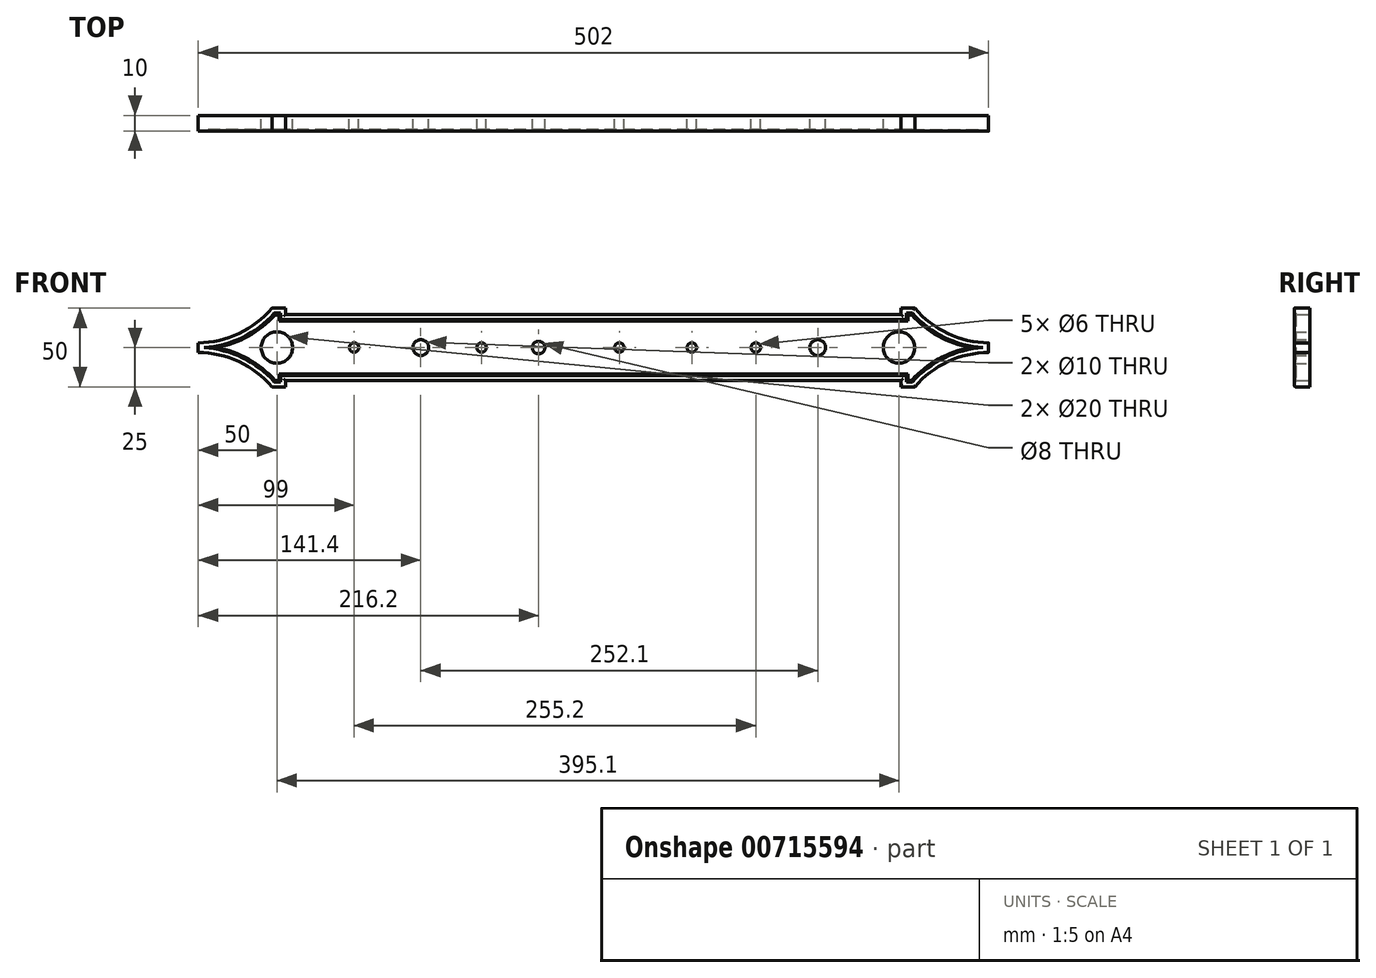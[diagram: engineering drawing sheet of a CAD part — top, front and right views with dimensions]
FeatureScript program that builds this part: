
annotation { "Feature Type Name" : "Feature", "Feature Type Description" : "" }
export const myFeature = defineFeature(function(context is Context, id is Id, definition is map)
    precondition{}
    {
        {
            var Q0;
            Q0=qCreatedBy(makeId("Front.planeOp"),FACE);
            var sketch = newSketch(context, id + "F0", { "sketchPlane" : qUnion([Q0])});
            skLineSegment(sketch, "E0.bottom", {"start": v(204.1, -25) * mm, "end": v(195.5, -25) * mm});
            skLineSegment(sketch, "E0.top", {"start": v(204.1, 25) * mm, "end": v(195.5, 25) * mm});
            skLineSegment(sketch, "E0.left", {"start": v(251, -3.05) * mm, "end": v(251, 3.05) * mm});
            skLineSegment(sketch, "E0.right", {"start": v(-251, -3.05) * mm, "end": v(-251, 3.05) * mm});
            skPoint(sketch, "E0.middle", {"position": v(0, 0) * mm});
            skLineSegment(sketch, "E1", {"start": v(-251, 3.05) * mm, "end": v(-251, -3.05) * mm});
            skLineSegment(sketch, "E2", {"start": v(251, 3.05) * mm, "end": v(251, -3.05) * mm});
            skLineSegment(sketch, "E3", {"start": v(-204.1, 25) * mm, "end": v(-195.5, 25) * mm});
            skLineSegment(sketch, "E4", {"start": v(-195.5, -25) * mm, "end": v(-204.1, -25) * mm});
            skArc(sketch, "E5", {"start": v(-251, 3.05) * mm, "mid": v(-225.17, 8.94) * mm, "end": v(-204.1, 25) * mm});
            skArc(sketch, "E6", {"start": v(-204.1, -25) * mm, "mid": v(-225.17, -8.94) * mm, "end": v(-251, -3.05) * mm});
            skPoint(sketch, "E7.orphan", {"position": v(-251, 25) * mm});
            skPoint(sketch, "E8.orphan", {"position": v(-251, -25) * mm});
            skArc(sketch, "E9", {"start": v(204.1, 25) * mm, "mid": v(225.17, 8.94) * mm, "end": v(251, 3.05) * mm});
            skArc(sketch, "E10", {"start": v(251, -3.05) * mm, "mid": v(225.17, -8.94) * mm, "end": v(204.1, -25) * mm});
            skPoint(sketch, "E11.orphan", {"position": v(251, 25) * mm});
            skPoint(sketch, "E12.orphan", {"position": v(251, -25) * mm});
            skLineSegment(sketch, "E13", {"start": v(195.5, 25) * mm, "end": v(195.5, 21) * mm});
            skLineSegment(sketch, "E14", {"start": v(195.5, -25) * mm, "end": v(195.5, -21) * mm});
            skLineSegment(sketch, "E15", {"start": v(-195.5, -25) * mm, "end": v(-195.5, -21) * mm});
            skLineSegment(sketch, "E16", {"start": v(-195.5, 25) * mm, "end": v(-195.5, 21) * mm});
            skLineSegment(sketch, "E17", {"start": v(-195.5, 21) * mm, "end": v(195.5, 21) * mm});
            skLineSegment(sketch, "E18", {"start": v(195.5, -21) * mm, "end": v(-195.5, -21) * mm});
            skLineSegment(sketch, "E19.trimOffspring", {"start": v(-195.5, 25) * mm, "end": v(-204.1, 25) * mm});
            skCircle(sketch, "E20", {"center": v(-201, 0) * mm, "radius": 10 * mm});
            skCircle(sketch, "E21", {"center": v(194.1, 0) * mm, "radius": 10 * mm});
            skCircle(sketch, "E22", {"center": v(142.5, 0) * mm, "radius": 5 * mm});
            skCircle(sketch, "E23", {"center": v(103.2, 0) * mm, "radius": 3 * mm});
            skCircle(sketch, "E24", {"center": v(62.5, 0) * mm, "radius": 3 * mm});
            skCircle(sketch, "E25", {"center": v(16.5, 0) * mm, "radius": 3 * mm});
            skCircle(sketch, "E26", {"center": v(-34.8, 0) * mm, "radius": 4 * mm});
            skCircle(sketch, "E27", {"center": v(-71, 0) * mm, "radius": 3 * mm});
            skCircle(sketch, "E28", {"center": v(-109.6, 0) * mm, "radius": 5 * mm});
            skCircle(sketch, "E29", {"center": v(-152, 0) * mm, "radius": 3 * mm});
            skLineSegment(sketch, "E30.0", {"start": v(-198.7, 21.8) * mm, "end": v(-198.7, 17.8) * mm});
            skLineSegment(sketch, "E30.1", {"start": v(-198.7, 21.8) * mm, "end": v(-202.65, 21.8) * mm});
            skArc(sketch, "E30.2", {"start": v(-247.32, 0) * mm, "mid": v(-222.84, 6.52) * mm, "end": v(-202.65, 21.8) * mm});
            skArc(sketch, "E30.4", {"start": v(-202.65, -21.81) * mm, "mid": v(-222.84, -6.52) * mm, "end": v(-247.32, 0) * mm});
            skArc(sketch, "E30.6", {"start": v(202.65, 21.81) * mm, "mid": v(222.84, 6.52) * mm, "end": v(247.32, 0) * mm});
            skLineSegment(sketch, "E30.7", {"start": v(202.65, 21.81) * mm, "end": v(198.7, 21.81) * mm});
            skLineSegment(sketch, "E30.8", {"start": v(198.7, 21.81) * mm, "end": v(198.7, 17.81) * mm});
            skArc(sketch, "E30.9", {"start": v(247.32, 0) * mm, "mid": v(222.84, -6.52) * mm, "end": v(202.65, -21.81) * mm});
            skLineSegment(sketch, "E30.10", {"start": v(202.65, -21.8) * mm, "end": v(198.7, -21.8) * mm});
            skLineSegment(sketch, "E30.11", {"start": v(198.7, -21.8) * mm, "end": v(198.7, -17.8) * mm});
            skLineSegment(sketch, "E30.12", {"start": v(198.7, -17.8) * mm, "end": v(-198.7, -17.81) * mm});
            skLineSegment(sketch, "E30.13", {"start": v(-198.7, -21.81) * mm, "end": v(-198.7, -17.81) * mm});
            skLineSegment(sketch, "E30.14", {"start": v(-198.7, 17.8) * mm, "end": v(198.7, 17.81) * mm});
            skLineSegment(sketch, "E30.15", {"start": v(-198.7, -21.81) * mm, "end": v(-202.65, -21.81) * mm});
            skLineSegment(sketch, "E31.0", {"start": v(199.7, 20.81) * mm, "end": v(199.7, 16.81) * mm});
            skLineSegment(sketch, "E31.1", {"start": v(-199.7, 16.8) * mm, "end": v(199.7, 16.81) * mm});
            skArc(sketch, "E31.2", {"start": v(202.2, 20.81) * mm, "mid": v(219.08, 7.36) * mm, "end": v(239.37, 0) * mm});
            skLineSegment(sketch, "E31.3", {"start": v(-199.7, 20.8) * mm, "end": v(-199.7, 16.8) * mm});
            skArc(sketch, "E31.4", {"start": v(-239.37, 0) * mm, "mid": v(-219.08, 7.36) * mm, "end": v(-202.2, 20.8) * mm});
            skArc(sketch, "E31.5", {"start": v(-202.2, -20.81) * mm, "mid": v(-219.08, -7.36) * mm, "end": v(-239.37, 0) * mm});
            skArc(sketch, "E31.6", {"start": v(239.37, 0) * mm, "mid": v(219.08, -7.36) * mm, "end": v(202.2, -20.81) * mm});
            skLineSegment(sketch, "E31.8", {"start": v(199.7, -16.8) * mm, "end": v(-199.7, -16.81) * mm});
            skLineSegment(sketch, "E31.9", {"start": v(-199.7, -20.81) * mm, "end": v(-199.7, -16.81) * mm});
            skLineSegment(sketch, "E32", {"start": v(199.7, 20.81) * mm, "end": v(202.2, 20.81) * mm});
            skLineSegment(sketch, "E33", {"start": v(199.7, -16.8) * mm, "end": v(199.7, -20.81) * mm});
            skLineSegment(sketch, "E34", {"start": v(199.7, -20.81) * mm, "end": v(202.2, -20.81) * mm});
            skLineSegment(sketch, "E35", {"start": v(-202.2, 20.8) * mm, "end": v(-199.7, 20.8) * mm});
            skLineSegment(sketch, "E36", {"start": v(-202.2, -20.81) * mm, "end": v(-199.7, -20.81) * mm});
            skSolve(sketch);
        }
        {
            var Q0;
            Q0 = qSketchRegion(id + "F0", true);
            var Q1;
            Q1=makeQuery(id+"F0.imprint","IMPRINT",FACE,{"disambiguationData":[TD([[makeQuery(id+"F0.imprint","IMPRINT",EDGE,{"derivedFrom":sQuery(id+"F0.wireOp",EDGE,"E20")}),-1.0]])]});
            extrude(context, id + "F1", {"entities" : qUnion([Q0, Q1]), "depth" : 10 * mm, "offsetDistance" : 25 * mm});
        }
        {
            var Q0;
            Q0=makeQuery(id+"F1.opExtrude","CAP_EDGE",EDGE,{"disambiguationData":[OSD([sQuery(id+"F0.wireOp",EDGE,"E17")])],"isStart":false});
            var Q1;
            Q1=makeQuery(id+"F1.opExtrude","CAP_EDGE",EDGE,{"disambiguationData":[OSD([sQuery(id+"F0.wireOp",EDGE,"E16")])],"isStart":false});
            var Q2;
            Q2=makeQuery(id+"F1.opExtrude","CAP_EDGE",EDGE,{"disambiguationData":[OSD([sQuery(id+"F0.wireOp",EDGE,"E1")])],"isStart":false});
            var Q3;
            Q3=makeQuery(id+"F1.opExtrude","CAP_EDGE",EDGE,{"disambiguationData":[OSD([sQuery(id+"F0.wireOp",EDGE,"E6")])],"isStart":false});
            var Q4;
            Q4=makeQuery(id+"F1.opExtrude","CAP_EDGE",EDGE,{"disambiguationData":[OSD([sQuery(id+"F0.wireOp",EDGE,"E4")])],"isStart":false});
            var Q5;
            Q5=makeQuery(id+"F1.opExtrude","CAP_EDGE",EDGE,{"disambiguationData":[OSD([sQuery(id+"F0.wireOp",EDGE,"E15")])],"isStart":false});
            var Q6;
            Q6=makeQuery(id+"F1.opExtrude","CAP_EDGE",EDGE,{"disambiguationData":[OSD([sQuery(id+"F0.wireOp",EDGE,"E18")])],"isStart":false});
            var Q7;
            Q7=makeQuery(id+"F1.opExtrude","CAP_EDGE",EDGE,{"disambiguationData":[OSD([sQuery(id+"F0.wireOp",EDGE,"E14")])],"isStart":false});
            var Q8;
            Q8=makeQuery(id+"F1.opExtrude","CAP_EDGE",EDGE,{"disambiguationData":[OSD([sQuery(id+"F0.wireOp",EDGE,"E0.bottom")])],"isStart":false});
            var Q9;
            Q9=makeQuery(id+"F1.opExtrude","CAP_EDGE",EDGE,{"disambiguationData":[OSD([sQuery(id+"F0.wireOp",EDGE,"E10")])],"isStart":false});
            var Q10;
            Q10=makeQuery(id+"F1.opExtrude","CAP_EDGE",EDGE,{"disambiguationData":[OSD([sQuery(id+"F0.wireOp",EDGE,"E2")])],"isStart":false});
            var Q11;
            Q11=makeQuery(id+"F1.opExtrude","CAP_EDGE",EDGE,{"disambiguationData":[OSD([sQuery(id+"F0.wireOp",EDGE,"E9")])],"isStart":false});
            var Q12;
            Q12=makeQuery(id+"F1.opExtrude","CAP_EDGE",EDGE,{"disambiguationData":[OSD([sQuery(id+"F0.wireOp",EDGE,"E0.top")])],"isStart":false});
            var Q13;
            Q13=makeQuery(id+"F1.opExtrude","CAP_EDGE",EDGE,{"disambiguationData":[OSD([sQuery(id+"F0.wireOp",EDGE,"E13")])],"isStart":false});
            var Q14;
            Q14=makeQuery(id+"F1.opExtrude","CAP_EDGE",EDGE,{"disambiguationData":[OSD([sQuery(id+"F0.wireOp",EDGE,"E19.trimOffspring")])],"isStart":false});
            var Q15;
            Q15=makeQuery(id+"F1.opExtrude","CAP_EDGE",EDGE,{"disambiguationData":[OSD([sQuery(id+"F0.wireOp",EDGE,"E5")])],"isStart":false});
            fillet(context, id + "F2", {"entities" : qUnion([Q0, Q1, Q2, Q3, Q4, Q5, Q6, Q7, Q8, Q9, Q10, Q11, Q12, Q13, Q14, Q15]), "radius" : 1 * mm, "tangentPropagation" : true, "allowEdgeOverflow" : false});
        }
        {
            var Q0;
            Q0=makeQuery(id+"F0.imprint","IMPRINT",FACE,{"disambiguationData":[TD([[makeQuery(id+"F0.imprint","IMPRINT",EDGE,{"derivedFrom":sQuery(id+"F0.wireOp",EDGE,"E30.0")}),-1.0]])]});
            extrude(context, id + "F3", {"entities" : qUnion([Q0]), "operationType" : NewBodyOperationType.ADD, "depth" : 9 * mm, "offsetDistance" : 25 * mm});
        }
    });
